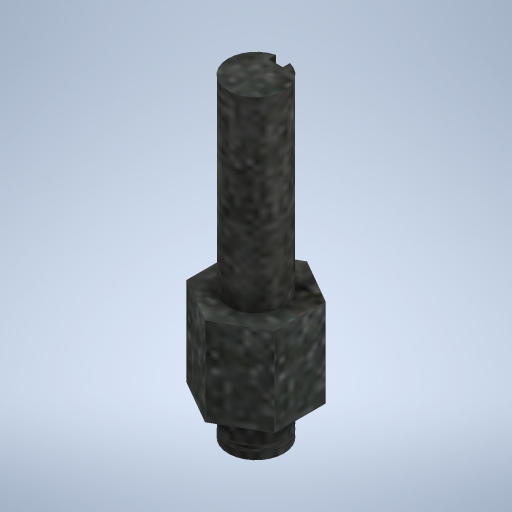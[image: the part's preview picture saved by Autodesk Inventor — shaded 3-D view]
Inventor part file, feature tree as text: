
AUTODESK INVENTOR PART (.ipt)
format: ipt  version: 2023 (Build 270158030, 158C)  size: 344,064 bytes
history: native  units: in
note: dims shown in document units (in); Inventor stores cm internally (conversion verified against a paired STEP export)
features: sketch x4, extrude x3, revolve x1
ambient origin geometry x8: Origin, YZ Plane, XZ Plane, XY Plane, X Axis, Y Axis, Z Axis, Center Point
bodies: Solid1 (feature_tree)
feature tree (8):
  extrude  "Extrusion1"  Depth=0.5in TaperAngle=0.0deg
  extrude  "Extrusion2"  Depth=1.0627in TaperAngle=0.0deg
  extrude  "Extrusion3"  Depth=0.081in
  revolve  "Revolution1"  [1 undecoded]
  sketch  "Sketch1"  dims[d0=0.5in d1=0.5in d2=0.0in]
  sketch  "Sketch2"  dims[d3=0.315in d4=1.0627in d5=0.0in]
  sketch  "Sketch3"  dims[d6=0.081in d8=0.046in]
  sketch  "Sketch4"  dims[d9=0.0in d10=0.0in d11=0.7195in d12=0.0in d13=0.0315in d14=0.2756in d15=90.0deg d16=0.0394in]
note: 1 required parameter value undecoded (feature->parameter linkage not recoverable at this tier; creation-order binding heuristic only, values carry confidence <= 0.55)
